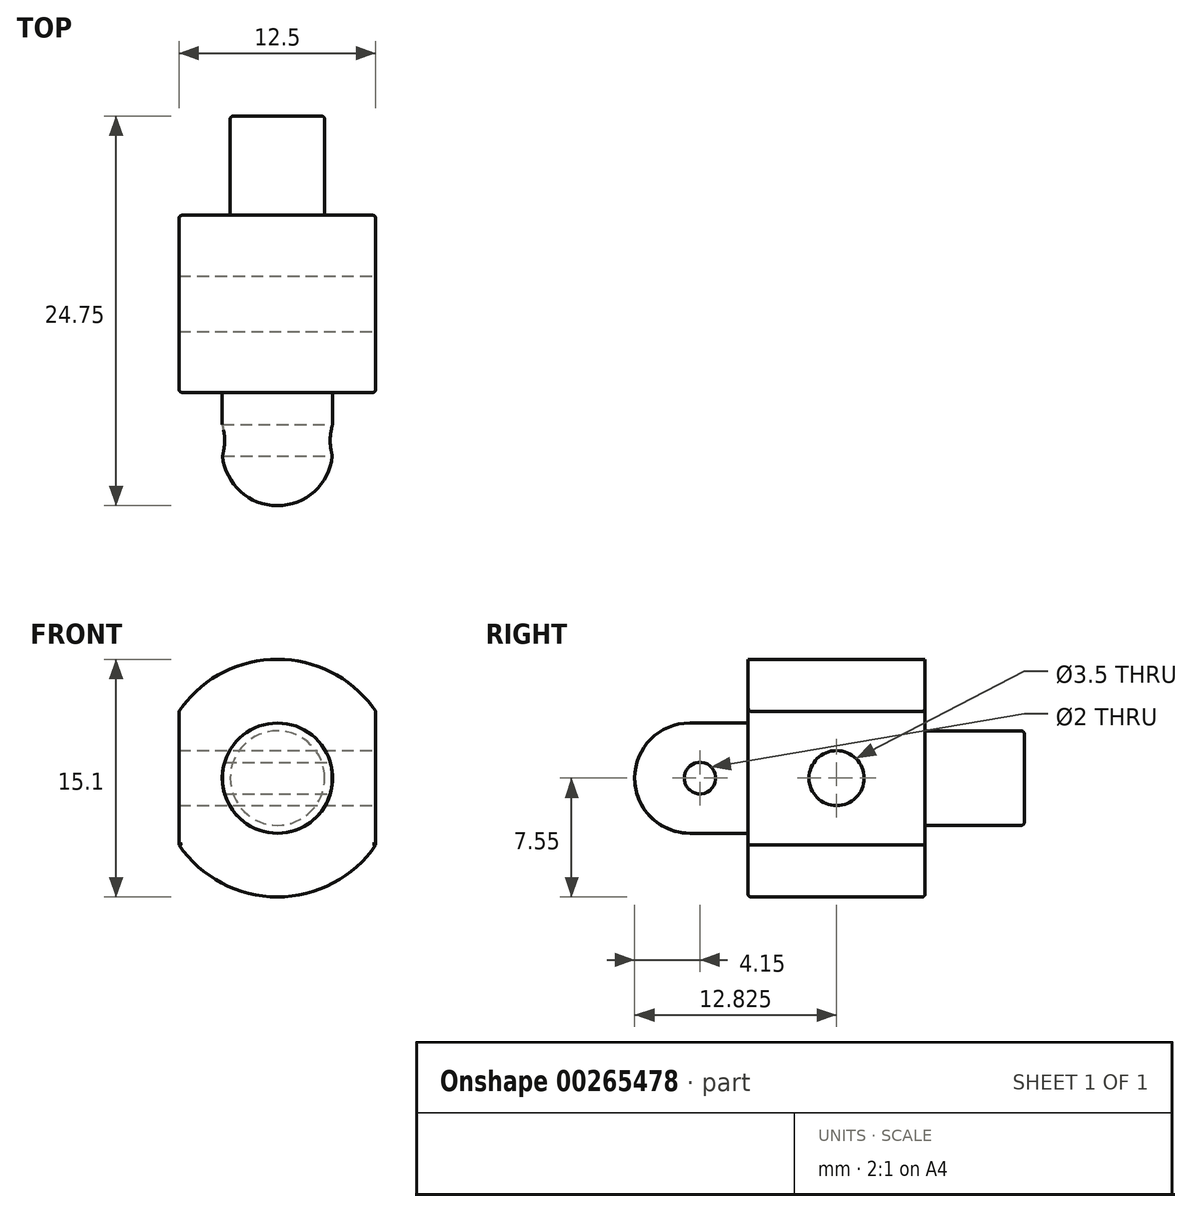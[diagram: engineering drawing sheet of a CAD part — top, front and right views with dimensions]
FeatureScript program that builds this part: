
annotation { "Feature Type Name" : "Feature", "Feature Type Description" : "" }
export const myFeature = defineFeature(function(context is Context, id is Id, definition is map)
    precondition{}
    {
        {
            var Q0;
            Q0=qCreatedBy(makeId("Front.planeOp"),FACE);
            var sketch = newSketch(context, id + "F0", { "sketchPlane" : qUnion([Q0])});
            skCircle(sketch, "E0", {"center": v(0, 0) * mm, "radius": 7.55 * mm});
            skLineSegment(sketch, "E1", {"start": v(0, 0) * mm, "end": v(12.5, 0) * mm, "construction": true});
            skLineSegment(sketch, "E2", {"start": v(12.5, 0) * mm, "end": v(-14.65, 0) * mm, "construction": true});
            skLineSegment(sketch, "E3", {"start": v(0, 0) * mm, "end": v(0, 11.46) * mm, "construction": true});
            skLineSegment(sketch, "E4", {"start": v(0, 11.46) * mm, "end": v(0, -11.2) * mm, "construction": true});
            skLineSegment(sketch, "E5", {"start": v(0, 0) * mm, "end": v(6.25, 0) * mm, "construction": true});
            skLineSegment(sketch, "E6", {"start": v(6.25, 0) * mm, "end": v(6.25, 4.24) * mm});
            skLineSegment(sketch, "E7", {"start": v(6.25, 4.24) * mm, "end": v(6.25, -4.24) * mm});
            skLineSegment(sketch, "E8.MirrorCS", {"start": v(-6.25, 4.24) * mm, "end": v(-6.25, -4.24) * mm});
            skSolve(sketch);
        }
        {
            var Q0;
            {var subQ5=sQuery(id+"F0.wireOp",EDGE,"E8.MirrorCS");Q0=makeQuery(id+"F0.imprint","IMPRINT",FACE,{"disambiguationData":[TD([[makeQuery(id+"F0.imprint","IMPRINT",EDGE,{"derivedFrom":subQ5}),1.0]])]});}
            extrude(context, id + "F1", {"entities" : qUnion([Q0]), "depth" : 11.25 * mm});
        }
        {
            var Q0;
            Q0=makeQuery(id+"F1.opExtrude","SWEPT_FACE",FACE,{"disambiguationData":[OSD([sQuery(id+"F0.wireOp",EDGE,"E7")])]});
            var sketch = newSketch(context, id + "F2", { "sketchPlane" : qUnion([Q0])});
            skLineSegment(sketch, "E9", {"start": v(0, 0) * mm, "end": v(-11.25, 0) * mm, "construction": true});
            skCircle(sketch, "E10", {"center": v(-5.62, 0) * mm, "radius": 1.75 * mm});
            skSolve(sketch);
        }
        {
            var Q0;
            Q0=makeQuery(id+"F2.imprint","IMPRINT",FACE,{"disambiguationData":[TD([[makeQuery(id+"F2.imprint","IMPRINT",EDGE,{"derivedFrom":sQuery(id+"F2.wireOp",EDGE,"E10")}),1.0]])]});
            extrude(context, id + "F3", {"entities" : qUnion([Q0]), "operationType" : NewBodyOperationType.REMOVE, "oppositeDirection" : true, "depth" : 15 * mm});
        }
        {
            var Q0;
            Q0=makeQuery(id+"F1.opExtrude","CAP_FACE",FACE,{"disambiguationData":[OSD([sQuery(id+"F0.wireOp",EDGE,"E0"),sQuery(id+"F0.wireOp",EDGE,"E7"),sQuery(id+"F0.wireOp",EDGE,"E8.MirrorCS")])],"isStart":true});
            var sketch = newSketch(context, id + "F4", { "sketchPlane" : qUnion([Q0])});
            skCircle(sketch, "E11", {"center": v(0, 0) * mm, "radius": 3 * mm});
            skSolve(sketch);
        }
        {
            var Q0;
            Q0=makeQuery(id+"F4.imprint","IMPRINT",FACE,{"disambiguationData":[TD([[makeQuery(id+"F4.imprint","IMPRINT",EDGE,{"derivedFrom":sQuery(id+"F4.wireOp",EDGE,"E11")}),1.0]])]});
            extrude(context, id + "F5", {"entities" : qUnion([Q0]), "operationType" : NewBodyOperationType.ADD, "depth" : 6.3 * mm});
        }
        {
            var Q0;
            Q0=makeQuery(id+"F1.opExtrude","CAP_FACE",FACE,{"disambiguationData":[OSD([sQuery(id+"F0.wireOp",EDGE,"E0"),sQuery(id+"F0.wireOp",EDGE,"E7"),sQuery(id+"F0.wireOp",EDGE,"E8.MirrorCS")])],"isStart":false});
            var sketch = newSketch(context, id + "F6", { "sketchPlane" : qUnion([Q0])});
            skCircle(sketch, "E12", {"center": v(0, 0) * mm, "radius": 3.5 * mm});
            skSolve(sketch);
        }
        {
            var Q0;
            Q0=makeQuery(id+"F6.imprint","IMPRINT",FACE,{"disambiguationData":[TD([[makeQuery(id+"F6.imprint","IMPRINT",EDGE,{"derivedFrom":sQuery(id+"F6.wireOp",EDGE,"E12")}),1.0]])]});
            extrude(context, id + "F7", {"entities" : qUnion([Q0]), "operationType" : NewBodyOperationType.ADD, "depth" : 7.2 * mm});
        }
        {
            var Q0;
            Q0=makeQuery(id+"F1.opExtrude","SWEPT_FACE",FACE,{"disambiguationData":[OSD([sQuery(id+"F0.wireOp",EDGE,"E7")])]});
            var sketch = newSketch(context, id + "F8", { "sketchPlane" : qUnion([Q0])});
            skLineSegment(sketch, "E13", {"start": v(0, 0) * mm, "end": v(-14.3, 0) * mm, "construction": true});
            skCircle(sketch, "E14", {"center": v(-14.3, 0) * mm, "radius": 1 * mm});
            skSolve(sketch);
        }
        {
            var Q0;
            Q0=makeQuery(id+"F8.imprint","IMPRINT",FACE,{"disambiguationData":[TD([[makeQuery(id+"F8.imprint","IMPRINT",EDGE,{"derivedFrom":sQuery(id+"F8.wireOp",EDGE,"E14")}),1.0]])]});
            extrude(context, id + "F9", {"entities" : qUnion([Q0]), "operationType" : NewBodyOperationType.REMOVE, "oppositeDirection" : true, "depth" : 15 * mm});
        }
        {
            var Q0;
            Q0=makeQuery(id+"F7.opExtrude","CAP_FACE",FACE,{"disambiguationData":[OSD([sQuery(id+"F6.wireOp",EDGE,"E12")])],"isStart":false});
            fillet(context, id + "F10", {"entities" : qUnion([Q0]), "radius" : 3.5 * mm, "tangentPropagation" : true, "allowEdgeOverflow" : false});
        }
        {
            var Q0;
            Q0=makeQuery(id+"F5.opExtrude","CAP_EDGE",EDGE,{"disambiguationData":[OSD([sQuery(id+"F4.wireOp",EDGE,"E11")])],"isStart":false});
            var Q1;
            {var subQ0=sQuery(id+"F0.wireOp",EDGE,"E0");Q1=makeQuery(id+"F1.opExtrude","CAP_EDGE",EDGE,{"disambiguationData":[OSD([subQ0]),TDD([makeQuery(id+"F0.imprint","IMPRINT",EDGE,{"disambiguationData":[TD([[makeQuery(id+"F0.imprint","INTERSECT",VERTEX,{"disambiguationData":[OD(0.0)],"derivedFrom":[subQ0,sQuery(id+"F0.wireOp",EDGE,"E7")]}),-1.0]])],"derivedFrom":subQ0})])],"isStart":true});}
            var Q2;
            Q2=makeQuery(id+"F1.opExtrude","CAP_EDGE",EDGE,{"disambiguationData":[OSD([sQuery(id+"F0.wireOp",EDGE,"E7")])],"isStart":true});
            var Q3;
            {var subQ0=sQuery(id+"F0.wireOp",EDGE,"E0");Q3=makeQuery(id+"F1.opExtrude","CAP_EDGE",EDGE,{"disambiguationData":[OSD([subQ0]),TDD([makeQuery(id+"F0.imprint","IMPRINT",EDGE,{"disambiguationData":[TD([[makeQuery(id+"F0.imprint","INTERSECT",VERTEX,{"disambiguationData":[OD(1.0)],"derivedFrom":[subQ0,sQuery(id+"F0.wireOp",EDGE,"E7")]}),1.0]])],"derivedFrom":subQ0})])],"isStart":true});}
            var Q4;
            Q4=makeQuery(id+"F1.opExtrude","CAP_EDGE",EDGE,{"disambiguationData":[OSD([sQuery(id+"F0.wireOp",EDGE,"E8.MirrorCS")])],"isStart":true});
            var Q5;
            {var subQ0=sQuery(id+"F0.wireOp",EDGE,"E0");Q5=makeQuery(id+"F1.opExtrude","CAP_EDGE",EDGE,{"disambiguationData":[OSD([subQ0]),TDD([makeQuery(id+"F0.imprint","IMPRINT",EDGE,{"disambiguationData":[TD([[makeQuery(id+"F0.imprint","INTERSECT",VERTEX,{"disambiguationData":[OD(0.0)],"derivedFrom":[subQ0,sQuery(id+"F0.wireOp",EDGE,"E7")]}),-1.0]])],"derivedFrom":subQ0})])],"isStart":false});}
            var Q6;
            {var subQ0=sQuery(id+"F0.wireOp",EDGE,"E0");Q6=makeQuery(id+"F1.opExtrude","CAP_EDGE",EDGE,{"disambiguationData":[OSD([subQ0]),TDD([makeQuery(id+"F0.imprint","IMPRINT",EDGE,{"disambiguationData":[TD([[makeQuery(id+"F0.imprint","INTERSECT",VERTEX,{"disambiguationData":[OD(1.0)],"derivedFrom":[subQ0,sQuery(id+"F0.wireOp",EDGE,"E7")]}),1.0]])],"derivedFrom":subQ0})])],"isStart":false});}
            var Q7;
            Q7=makeQuery(id+"F1.opExtrude","CAP_EDGE",EDGE,{"disambiguationData":[OSD([sQuery(id+"F0.wireOp",EDGE,"E8.MirrorCS")])],"isStart":false});
            var Q8;
            Q8=makeQuery(id+"F1.opExtrude","CAP_EDGE",EDGE,{"disambiguationData":[OSD([sQuery(id+"F0.wireOp",EDGE,"E7")])],"isStart":false});
            fillet(context, id + "F11", {"entities" : qUnion([Q0, Q1, Q2, Q3, Q4, Q5, Q6, Q7, Q8]), "radius" : 0.2 * mm, "tangentPropagation" : true, "allowEdgeOverflow" : false});
        }
    });
